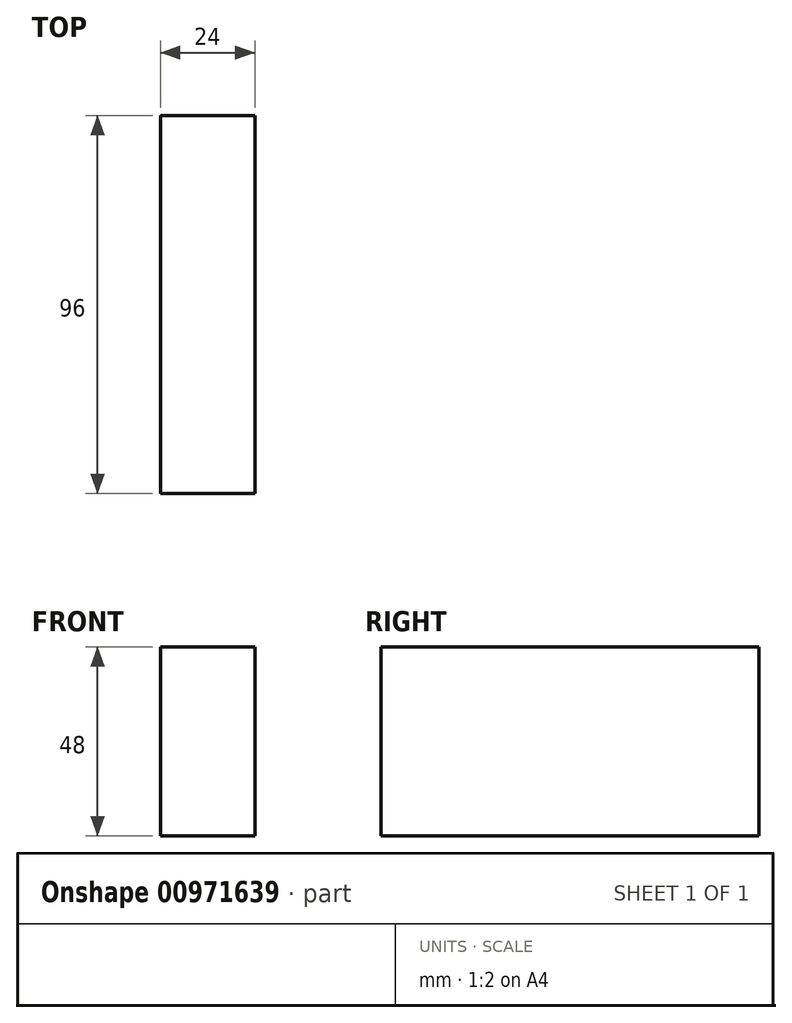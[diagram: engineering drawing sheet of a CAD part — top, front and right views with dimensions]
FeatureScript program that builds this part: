
annotation { "Feature Type Name" : "Feature", "Feature Type Description" : "" }
export const myFeature = defineFeature(function(context is Context, id is Id, definition is map)
    precondition{}
    {
        {
            assignVariable(context, id + "F0", {"name" : "c", "anyValue" : 96});
        }
        {
            var Q0;
            Q0=qCreatedBy(makeId("Front.planeOp"),FACE);
            var sketch = newSketch(context, id + "F1", { "sketchPlane" : qUnion([Q0])});
            skLineSegment(sketch, "E0.bottom", {"start": v(12, -24) * mm, "end": v(-12, -24) * mm});
            skLineSegment(sketch, "E0.top", {"start": v(12, 24) * mm, "end": v(-12, 24) * mm});
            skLineSegment(sketch, "E0.left", {"start": v(12, -24) * mm, "end": v(12, 24) * mm});
            skLineSegment(sketch, "E0.right", {"start": v(-12, -24) * mm, "end": v(-12, 24) * mm});
            skPoint(sketch, "E0.middle", {"position": v(0, 0) * mm});
            skSolve(sketch);
        }
        {
            var Q0;
            Q0=qSketchRegion(id+"F1",true);
            var Q1;
            Q1=makeQuery(id+"F1.imprint","IMPRINT",FACE,{"disambiguationData":[TD([[makeQuery(id+"F1.imprint","IMPRINT",EDGE,{"derivedFrom":sQuery(id+"F1.wireOp",EDGE,"E0.bottom")}),-1.0]])]});
            extrude(context, id + "F2", {"entities" : qUnion([Q0, Q1]), "depth" : (getVariable(context, 'c')) * mm, "offsetDistance" : 25 * mm});
        }
    });
